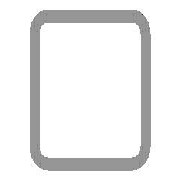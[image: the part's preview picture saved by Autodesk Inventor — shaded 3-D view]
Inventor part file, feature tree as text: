
AUTODESK INVENTOR PART (.ipt)
format: ipt  version: 2025 (Build 290162010, 162A)  size: 133,632 bytes
history: native  units: mm (DEFAULTED — no unit token found)
features: other x4, sketch x1, plane x1
ambient origin geometry x8: Origin, YZ Plane, XZ Plane, XY Plane, X Axis, Y Axis, Z Axis, Center Point
bodies: Solid1 (feature_tree), Body (feature_tree)
feature tree (6):
  parser-record x1  (decoder bookkeeping rows leaked as tree rows — omitted from the tree; the rows remain in map.json)
  other  "Driven Length"
  other  "Start Plane"
  other  "End Plane"
  sketch  "Sketch3"  dims[d3=1420.0mm d4=0.0mm d7=4.0mm d9=40.0mm d11=40.0mm d12=2.0mm d13=40.0mm d14=1460.0mm d15=20.0mm d16=20.0mm d17=90.0deg d18=1420.0mm]
  plane  "Work Plane3"
